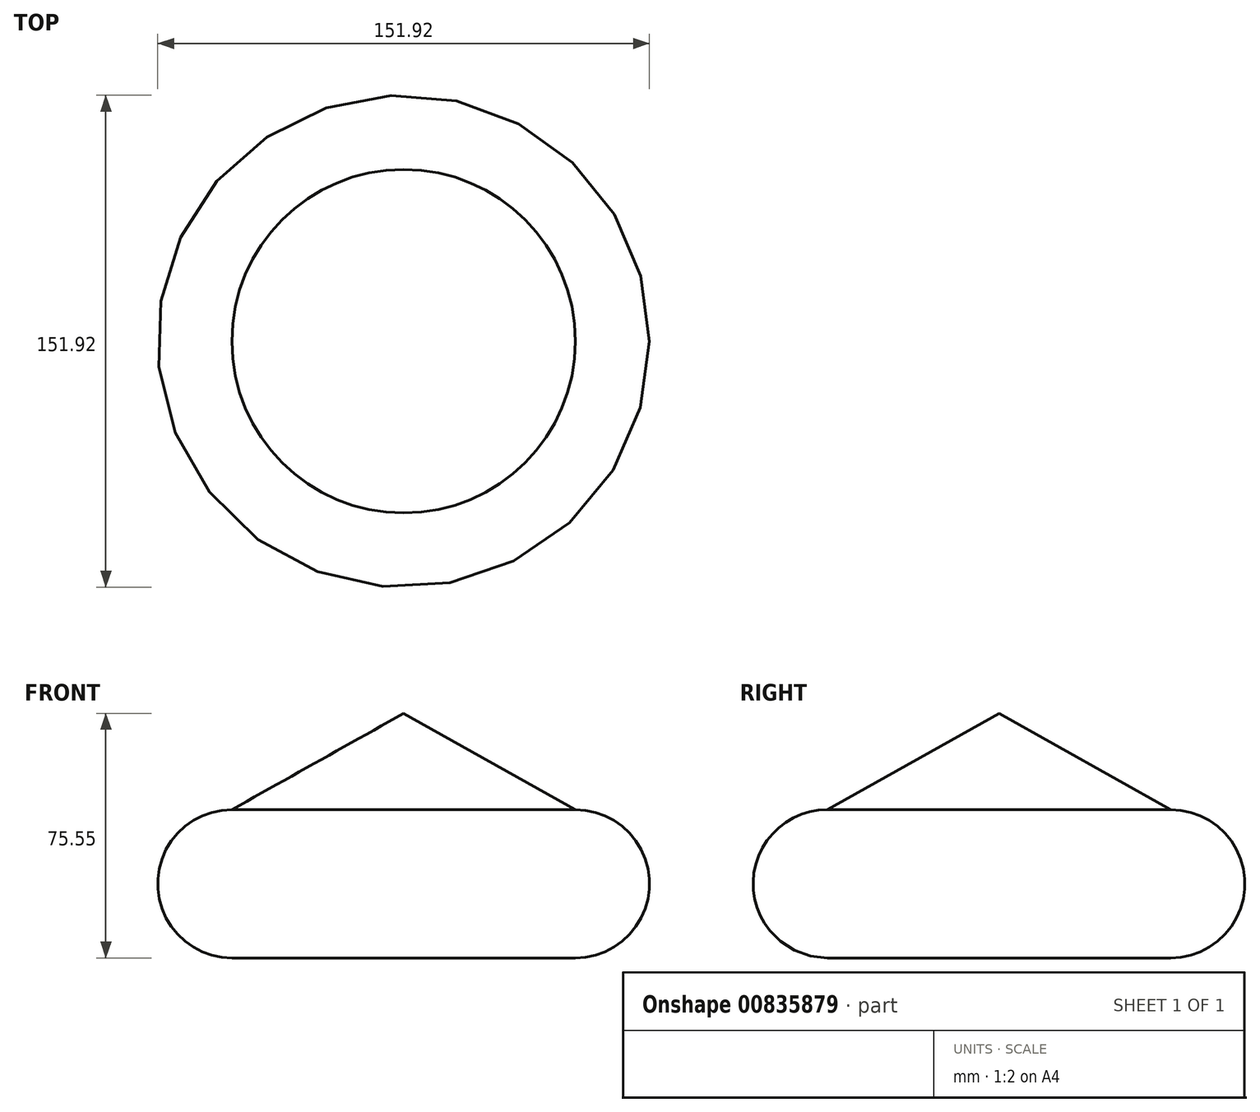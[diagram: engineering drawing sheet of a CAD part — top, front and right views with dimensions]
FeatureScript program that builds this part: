
annotation { "Feature Type Name" : "Feature", "Feature Type Description" : "" }
export const myFeature = defineFeature(function(context is Context, id is Id, definition is map)
    precondition{}
    {
        {
            var Q0;
            Q0=qCreatedBy(makeId("Front.planeOp"),FACE);
            var sketch = newSketch(context, id + "F0", { "sketchPlane" : qUnion([Q0])});
            skLineSegment(sketch, "E0", {"start": v(53.06, 45.8) * mm, "end": v(0, 75.55) * mm});
            skLineSegment(sketch, "E1", {"start": v(53.06, 0) * mm, "end": v(0, -16.37) * mm});
            skArc(sketch, "E2", {"start": v(53.06, 45.8) * mm, "mid": v(75.96, 22.9) * mm, "end": v(53.06, 0) * mm});
            skLineSegment(sketch, "E3", {"start": v(0, 75.55) * mm, "end": v(0, -16.37) * mm});
            skSolve(sketch);
        }
        {
            var Q0;
            Q0=makeQuery(id+"F0.imprint","IMPRINT",FACE,{"disambiguationData":[TD([[makeQuery(id+"F0.imprint","IMPRINT",EDGE,{"derivedFrom":sQuery(id+"F0.wireOp",EDGE,"E0")}),1.0]])]});
            var Q1;
            Q1=sQuery(id+"F0.wireOp",EDGE,"E3");
            revolve(context, id + "F1", {"surfaceOperationType" : NewSurfaceOperationType.NEW, "entities" : qUnion([Q0]), "axis" : qUnion([Q1]), "revolveType" : RevolveType.FULL});
        }
        {
            var Q0;
            Q0=qCreatedBy(makeId("Top.planeOp"),FACE);
            var sketch = newSketch(context, id + "F2", { "sketchPlane" : qUnion([Q0])});
            skCircle(sketch, "E4", {"center": v(0, 0) * mm, "radius": 53.42 * mm});
            skSolve(sketch);
        }
        {
            var Q0;
            Q0 = qSketchRegion(id + "F2", true);
            extrude(context, id + "F3", {"entities" : qUnion([Q0]), "operationType" : NewBodyOperationType.REMOVE, "oppositeDirection" : true, "depth" : 25.4 * mm, "offsetDistance" : 25.4 * mm});
        }
    });
